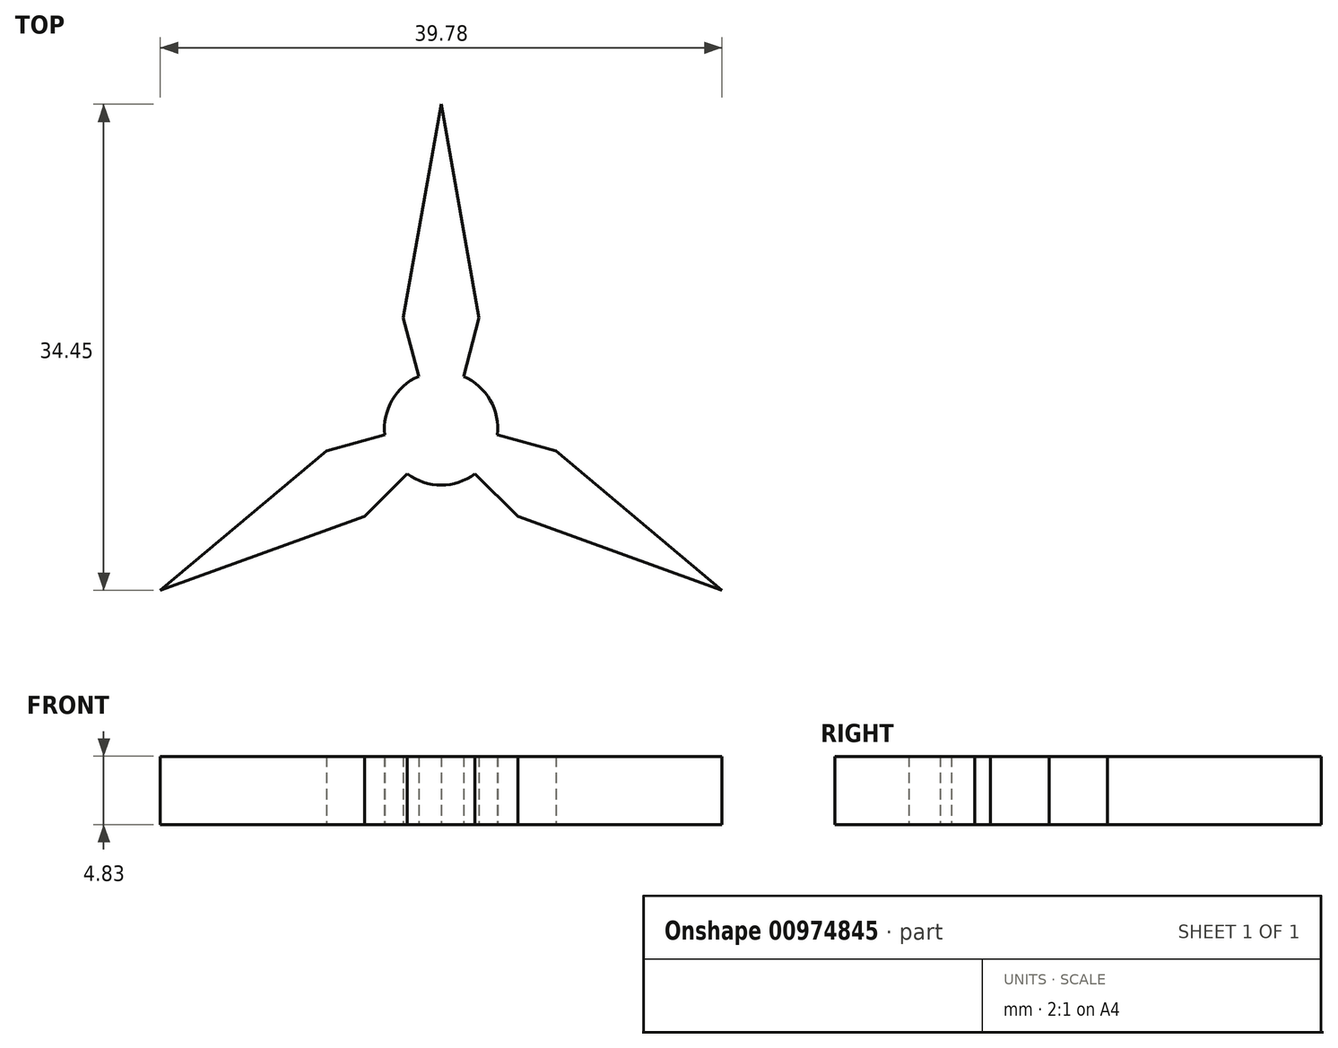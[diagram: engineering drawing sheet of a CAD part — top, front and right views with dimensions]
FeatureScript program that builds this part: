
annotation { "Feature Type Name" : "Feature", "Feature Type Description" : "" }
export const myFeature = defineFeature(function(context is Context, id is Id, definition is map)
    precondition{}
    {
        {
            var Q0;
            Q0=qCreatedBy(makeId("Top.planeOp"),FACE);
            var sketch = newSketch(context, id + "F0", { "sketchPlane" : qUnion([Q0])});
            skCircle(sketch, "E0", {"center": v(0, 0) * mm, "radius": 4.01 * mm});
            skLineSegment(sketch, "E1", {"start": v(-1.59, 3.68) * mm, "end": v(-2.69, 7.83) * mm});
            skLineSegment(sketch, "E2", {"start": v(-2.69, 7.83) * mm, "end": v(-1.6, 13.95) * mm});
            skLineSegment(sketch, "E3", {"start": v(-1.6, 13.95) * mm, "end": v(0, 22.97) * mm});
            skLineSegment(sketch, "E4", {"start": v(0, 22.97) * mm, "end": v(0, 4.01) * mm});
            skLineSegment(sketch, "E5.MirrorCS", {"start": v(1.6, 13.95) * mm, "end": v(0, 22.97) * mm});
            skLineSegment(sketch, "E6.MirrorCS", {"start": v(2.69, 7.83) * mm, "end": v(1.6, 13.95) * mm});
            skLineSegment(sketch, "E7.MirrorCS", {"start": v(1.59, 3.68) * mm, "end": v(2.69, 7.83) * mm});
            skLineSegment(sketch, "E8.1.0", {"start": v(-3.98, -0.46) * mm, "end": v(-8.12, -1.59) * mm});
            skLineSegment(sketch, "E8.1.1", {"start": v(-2.4, -3.22) * mm, "end": v(-5.43, -6.24) * mm});
            skLineSegment(sketch, "E8.1.2", {"start": v(-5.43, -6.24) * mm, "end": v(-11.28, -8.36) * mm});
            skLineSegment(sketch, "E8.1.3", {"start": v(-8.12, -1.59) * mm, "end": v(-12.88, -5.59) * mm});
            skLineSegment(sketch, "E8.1.4", {"start": v(-11.28, -8.36) * mm, "end": v(-19.89, -11.48) * mm});
            skLineSegment(sketch, "E8.1.5", {"start": v(-12.88, -5.59) * mm, "end": v(-19.89, -11.48) * mm});
            skLineSegment(sketch, "E8.2.0", {"start": v(2.4, -3.22) * mm, "end": v(5.43, -6.24) * mm});
            skLineSegment(sketch, "E8.2.1", {"start": v(3.98, -0.46) * mm, "end": v(8.12, -1.59) * mm});
            skLineSegment(sketch, "E8.2.2", {"start": v(8.12, -1.59) * mm, "end": v(12.88, -5.59) * mm});
            skLineSegment(sketch, "E8.2.3", {"start": v(5.43, -6.24) * mm, "end": v(11.28, -8.36) * mm});
            skLineSegment(sketch, "E8.2.4", {"start": v(12.88, -5.59) * mm, "end": v(19.89, -11.48) * mm});
            skLineSegment(sketch, "E8.2.5", {"start": v(11.28, -8.36) * mm, "end": v(19.89, -11.48) * mm});
            skSolve(sketch);
        }
        {
            var Q0;
            {var subQ1=sQuery(id+"F0.wireOp",EDGE,"E8.1.0");Q0=makeQuery(id+"F0.imprint","IMPRINT",FACE,{"disambiguationData":[TD([[makeQuery(id+"F0.imprint","IMPRINT",EDGE,{"derivedFrom":subQ1}),1.0]])]});}
            var Q1;
            {var subQ1=sQuery(id+"F0.wireOp",EDGE,"E8.2.0");Q1=makeQuery(id+"F0.imprint","IMPRINT",FACE,{"disambiguationData":[TD([[makeQuery(id+"F0.imprint","IMPRINT",EDGE,{"derivedFrom":subQ1}),1.0]])]});}
            var Q2;
            {var subQ0=sQuery(id+"F0.wireOp",EDGE,"E4");Q2=makeQuery(id+"F0.imprint","IMPRINT",FACE,{"disambiguationData":[TD([[makeQuery(id+"F0.imprint","IMPRINT",EDGE,{"derivedFrom":subQ0}),1.0]])]});}
            var Q3;
            {var subQ0=sQuery(id+"F0.wireOp",EDGE,"E0");var subQ4=makeQuery(id+"F0.imprint","INTERSECT",VERTEX,{"derivedFrom":[subQ0,sQuery(id+"F0.wireOp",EDGE,"E4")]});Q3=makeQuery(id+"F0.imprint","IMPRINT",FACE,{"disambiguationData":[TD([[makeQuery(id+"F0.imprint","IMPRINT",EDGE,{"disambiguationData":[TD([[subQ4,1.0]])],"derivedFrom":subQ0}),1.0]])]});}
            var Q4;
            {var subQ0=sQuery(id+"F0.wireOp",EDGE,"E1");Q4=makeQuery(id+"F0.imprint","IMPRINT",FACE,{"disambiguationData":[TD([[makeQuery(id+"F0.imprint","IMPRINT",EDGE,{"derivedFrom":subQ0}),-1.0]])]});}
            extrude(context, id + "F1", {"entities" : qUnion([Q0, Q1, Q2, Q3, Q4]), "depth" : 4.83 * mm, "offsetDistance" : 25.4 * mm});
        }
    });
